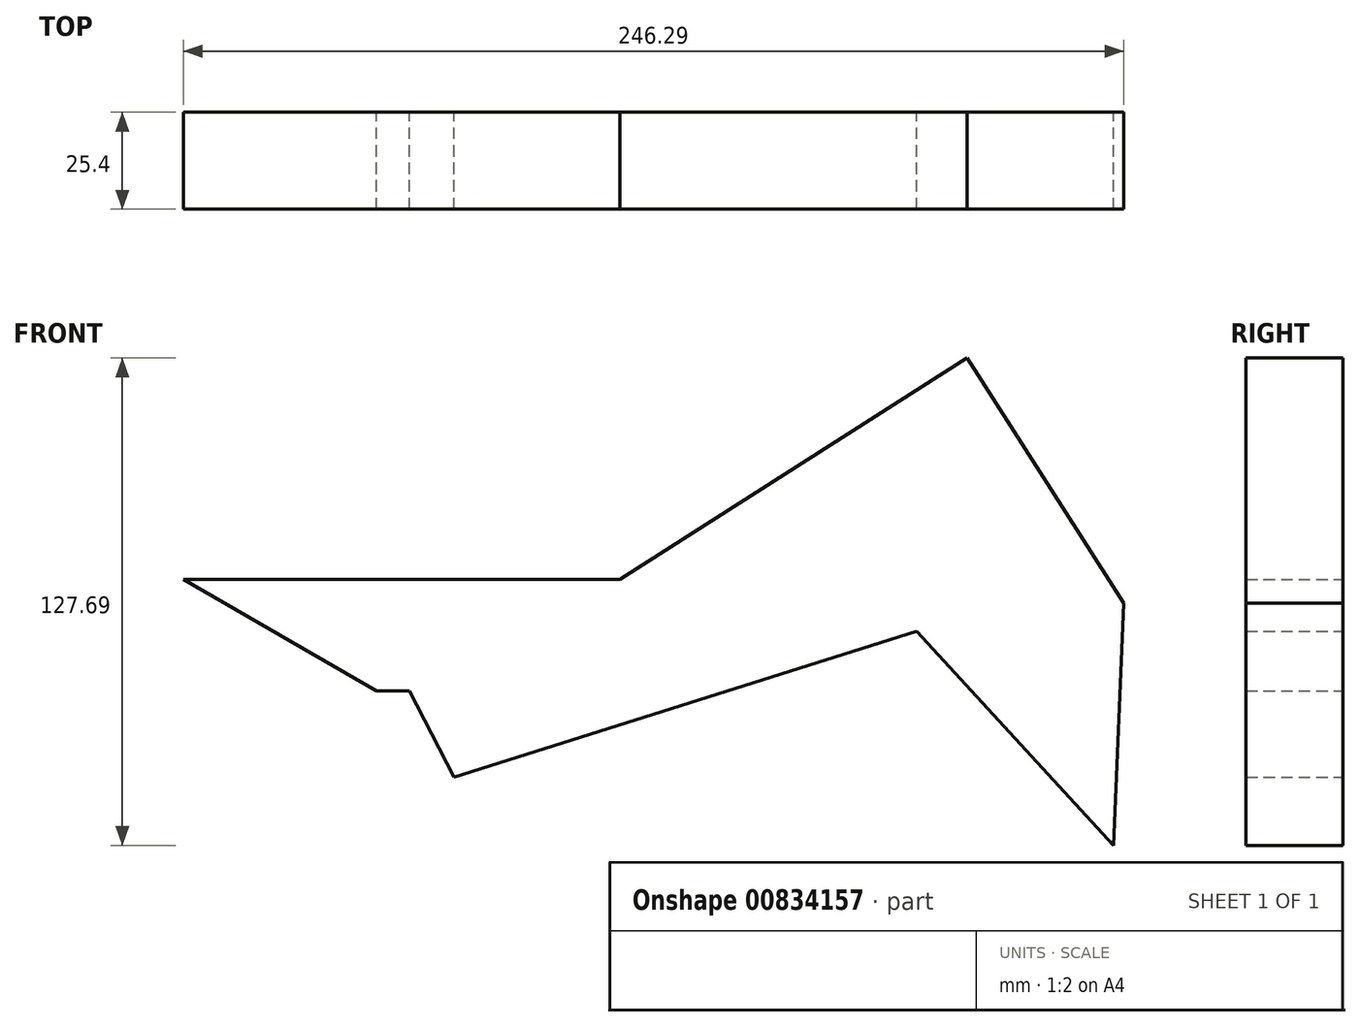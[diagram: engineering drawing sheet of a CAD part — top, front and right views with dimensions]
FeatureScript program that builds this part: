
annotation { "Feature Type Name" : "Feature", "Feature Type Description" : "" }
export const myFeature = defineFeature(function(context is Context, id is Id, definition is map)
    precondition{}
    {
        {
            var Q0;
            Q0=qCreatedBy(makeId("Front.planeOp"),FACE);
            var sketch = newSketch(context, id + "F0", { "sketchPlane" : qUnion([Q0])});
            skLineSegment(sketch, "E0", {"start": v(0, 0) * mm, "end": v(-50.6, 29.2) * mm});
            skLineSegment(sketch, "E1", {"start": v(-50.6, 29.2) * mm, "end": v(63.7, 29.2) * mm});
            skLineSegment(sketch, "E2", {"start": v(63.7, 29.2) * mm, "end": v(154.72, 87.26) * mm});
            skLineSegment(sketch, "E3", {"start": v(154.72, 87.26) * mm, "end": v(195.7, 23) * mm});
            skLineSegment(sketch, "E4", {"start": v(195.7, 23) * mm, "end": v(192.96, -40.43) * mm});
            skLineSegment(sketch, "E5", {"start": v(192.96, -40.43) * mm, "end": v(141.45, 15.72) * mm});
            skLineSegment(sketch, "E6", {"start": v(141.45, 15.72) * mm, "end": v(20.35, -22.52) * mm});
            skLineSegment(sketch, "E7", {"start": v(20.35, -22.52) * mm, "end": v(8.6, 0) * mm});
            skLineSegment(sketch, "E8", {"start": v(8.6, 0) * mm, "end": v(0, 0) * mm});
            skSolve(sketch);
        }
        {
            var Q0;
            Q0 = qSketchRegion(id + "F0", true);
            extrude(context, id + "F1", {"entities" : qUnion([Q0]), "depth" : 25.4 * mm, "offsetDistance" : 25.4 * mm});
        }
    });
